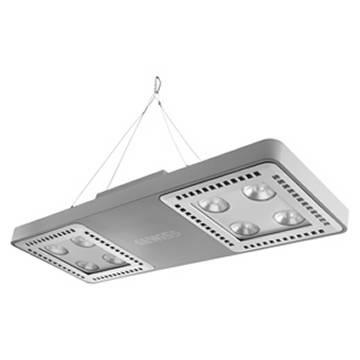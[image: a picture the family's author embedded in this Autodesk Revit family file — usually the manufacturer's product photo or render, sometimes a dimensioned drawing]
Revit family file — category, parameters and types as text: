
# Revit family: Lighting-Industrial-GEWISS-SMART[4]HLO_HIGHBAYS-LED_2M
name_source: partatom
category: Apparecchi per illuminazione
units: mm (PartAtom-declared; Revit-internal decimal feet)

## family parameters
Basato su piano di lavoro = Sì
Condiviso = No
Numero OmniClass = 23.80.70.00
Punto di calcolo locali = No
Quota connettore circolare = Usa diametro
Sempre verticale = No
Sorgente d'illuminazione = No
Taglio con vuoti quando caricato = No
Tipo di parte = Normale
Titolo OmniClass = Lighting

## types (36) — shared parameters
Application = Internal
Body = PA6 "Halogen Free" loaded fibreglass
Carico apparente = 97 VA
Catalogue = LIGHTING
Classification: = -
Classificazione = Lighting
Color Rendering Index = CRI-80
Colour = Grey RAL 7035
Colour : = Grey RAL 7035
Commenti sul wattaggio = 97W
Context = Lighting for industries and sports facilities
Control System = ON / OFF
Control System : = ON / OFF
DIN 18032-3 certification = With Bracket - Rope Kit + terminal&nbsp;(in approval)
Device with reduced surface temperature = Yes
Dist_sorg_lum = 10 mm  [stored 0.0328084 ft]
Driver = Included
Driver Box = Built-in
Electrocod = 2444
Eletrical and lighting features = -
External screw = Stainless steel
Fixing = -
Gasket = anti-aging silicone
General information = -
Glow Wire Test : = 850 °C
IDF = 87744efe-63fb-4f16-8ca3-e5681c99f1f6
IDT = d6c0a54b56be4af78e01cdd4bdcb8af8
IP degree = IP66
IPEA = -
Immagine tipo = GWL1311.jpg
Installationa and maintenance = -
Insulation class = I
LED Maintenance = Non-replaceable
Lampada = LED
Larghezza = 254 mm
Lifetime = L90B10 (Tq+25°C) = 70.000 h - L90B10 (Tq+50°C) = 35.000 h
Locking Hook = -
Luminaire = LED Industrial ReflectorÂ
Lunghezza = 699 mm  [stored 2.29331 ft]
Mascherina = <Per categoria>
Materials = -
Maximum surface exposed to the wind : = 0,184 m²
Motore = <Per categoria>
Mouting and installation = Ceiling - Wallmounting - Suspension
Operating temperature : = -30°C ÷ +50 °C
Optic Maintenance = Non-replaceable
Optic and illuminating features = -
Overvoltage protection = DM 6kV / CM 6kV
Photobiological Risk Class = RG0
Produttore = GEWISS S.p.A.
Prospetto di default = 1219 mm
Rated frequency (Hz) = 50/60 Hz
Shield type = Tempered glass Thickness 4mm
Shock resistance = IK08
Spessore plafoniera = 40 mm  [stored 0.131234 ft]
Standard Deviation Colour Matching = SDCM = 3
Standard- = EN 60598-1 ; EN 60598-2-1 ; EN 60598-2-24
Standards and approvals = -
Stocking temperature = -40 +70 °C
Struttura plafoniera = <Per categoria>
Supply voltage = 220 - 240 V
System power = 125W
Technical sheet = https://www.gewiss.com
Tilt- = With bracket accessory
Trasformatore = <Per categoria>
Type of light source = LED - Not replaceable
URL = https://www.gewiss.com
Unique digital code (Datamatrix) = Datamatrix
Version file RFA = 20.11
Voltaggio = 230 V
Warranty = 5 years
Weight (kg): = 6,5
Wiring = With GW connect watertight connector

## per-type parameters (varying)
| type | Colour temperature | Descrizione | Efficiency (lm/W) | Lumen output (lm) | Modello | Optic | Optic : | SEO | Unified Glare Rating |
| GWS4222BF840 - SMART4HB 2M C.PAS.ON/OFF HLO 30° 40K | 4000K | SMART[4]HB 2M C.PAS.ON/OFF HLO 30° 40K | 141 | 17600 | GWS4222BF840 | 30° | Metallic PC reflector and PMMA lenses |  | UGR - 19 |
| GWS4220BC840 - SMART4HB 2M ST.AL.ON/OFF HLO ASI.40K | 4000K | SMART[4]HB 2M ST.AL.ON/OFF HLO ASI.40K | 128 | 16000 | GWS4220BC840 | Asymmetrical | Metallic PC reflector and PMMA lenses | High bay | - |
| GWS4222BC857 - SMART4HB 2M C.PAS.ON/OFF HLO ASI.57K | 5700K | SMART[4]HB 2M C.PAS.ON/OFF HLO ASI.57K | 128 | 16000 | GWS4222BC857 | Asymmetrical | Metallic PC reflector and PMMA lenses | High bay | - |
| GWS4220BP857 - SMART4HB 2M ST.AL.ON/OFF HLO 90° 57K | 5700K | SMART[4]HB 2M ST.AL.ON/OFF HLO 90° 57K | 144 | 18000 | GWS4220BP857 | 90° | Metallic PC reflector and PMMA lenses |  | UGR - 25 |
| GWS4222BF857 - SMART4HB 2M C.PAS.ON/OFF HLO 30° 57K | 5700K | SMART[4]HB 2M C.PAS.ON/OFF HLO 30° 57K | 141 | 17600 | GWS4222BF857 | 30° | Metallic PC reflector and PMMA lenses |  | UGR - 19 |
| GWS4220BH830 - SMART4HB 2M ST.AL.ON/OFF HLO 60° 30K | 3000K | SMART[4]HB 2M ST.AL.ON/OFF HLO 60° 30K | 135 | 16900 | GWS4220BH830 | 60° | Metallic PC reflector and PMMA lenses |  | UGR - 22 |
| GWS4220BQ857 - SMART4HB 2M ST.AL.ON/OFF HLO ELL.57K | 5700K | SMART[4]HB 2M ST.AL.ON/OFF HLO ELL.57K | 128 | 16000 | GWS4220BQ857 | Elliptical | Metallic PC reflector and PMMA lenses | High bay | - |
| GWS4220BF857 - SMART4HB 2M ST.AL.ON/OFF HLO 30° 57K | 5700K | SMART[4]HB 2M ST.AL.ON/OFF HLO 30° 57K | 141 | 17600 | GWS4220BF857 | 30° | Metallic PC reflector and PMMA lenses |  | UGR - 19 |
| GWS4220BF840 - SMART4HB 2M ST.AL.ON/OFF HLO 30° 40K | 4000K | SMART[4]HB 2M ST.AL.ON/OFF HLO 30° 40K | 141 | 17600 | GWS4220BF840 | 30° | Metallic PC reflector and PMMA lenses |  | UGR - 19 |
| GWS4220BA840 - SMART4HB 2M ST.AL.ON/OFF HLO ARR.40K | 4000K | SMART[4]HB 2M ST.AL.ON/OFF HLO ARR.40K | 144 | 18000 | GWS4220BA840 | Array | Metallized polycarbonate reflector |  | - |
| GWS4222BH840 - SMART4HB 2M C.PAS.ON/OFF HLO 60° 40K | 4000K | SMART[4]HB 2M C.PAS.ON/OFF HLO 60° 40K | 142 | 17700 | GWS4222BH840 | 60° | Metallic PC reflector and PMMA lenses |  | UGR - 22 |
| GWS4222BA840 - SMART4HB 2M C.PAS.ON/OFF HLO ARR.40K | 4000K | SMART[4]HB 2M C.PAS.ON/OFF HLO ARR.40K | 144 | 18000 | GWS4222BA840 | Array | Metallized polycarbonate reflector |  | - |
| GWS4220BC857 - SMART4HB 2M ST.AL.ON/OFF HLO ASI.57K | 5700K | SMART[4]HB 2M ST.AL.ON/OFF HLO ASI.57K | 128 | 16000 | GWS4220BC857 | Asymmetrical | Metallic PC reflector and PMMA lenses | High bay | - |
| GWS4220BA830 - SMART4HB 2M ST.AL.ON/OFF HLO ARR.30K | 3000K | SMART[4]HB 2M ST.AL.ON/OFF HLO ARR.30K | 138 | 17200 | GWS4220BA830 | Array | Metallized polycarbonate reflector |  | - |
| GWS4222BP857 - SMART4HB 2M C.PAS.ON/OFF HLO 90° 57K | 5700K | SMART[4]HB 2M C.PAS.ON/OFF HLO 90° 57K | 144 | 18000 | GWS4222BP857 | 90° | Metallic PC reflector and PMMA lenses |  | UGR - 25 |
| GWS4222BF830 - SMART4HB 2M C.PAS.ON/OFF HLO 30° 30K | 3000K | SMART[4]HB 2M C.PAS.ON/OFF HLO 30° 30K | 134 | 16800 | GWS4222BF830 | 30° | Metallic PC reflector and PMMA lenses |  | UGR - 19 |
| GWS4222BC840 - SMART4HB 2M C.PAS.ON/OFF HLO ASI.40K | 4000K | SMART[4]HB 2M C.PAS.ON/OFF HLO ASI.40K | 128 | 16000 | GWS4222BC840 | Asymmetrical | Metallic PC reflector and PMMA lenses | High bay | - |
| GWS4222BH857 - SMART4HB 2M C.PAS.ON/OFF HLO 60° 57K | 5700K | SMART[4]HB 2M C.PAS.ON/OFF HLO 60° 57K | 142 | 17700 | GWS4222BH857 | 60° | Metallic PC reflector and PMMA lenses |  | UGR - 22 |
| GWS4220BQ830 - SMART4HB 2M ST.AL.ON/OFF HLO ELL.30K | 3000K | SMART[4]HB 2M ST.AL.ON/OFF HLO ELL.30K | 122 | 15300 | GWS4220BQ830 | Elliptical | Metallic PC reflector and PMMA lenses | High bay | - |
| GWS4222BA857 - SMART4HB 2M C.PAS.ON/OFF HLO ARR.57K | 5700K | SMART[4]HB 2M C.PAS.ON/OFF HLO ARR.57K | 144 | 18000 | GWS4222BA857 | Array | Metallized polycarbonate reflector |  | - |
| GWS4222BQ857 - SMART4HB 2M C.PAS.ON/OFF HLO ELL.57K | 5700K | SMART[4]HB 2M C.PAS.ON/OFF HLO ELL.57K | 128 | 16000 | GWS4222BQ857 | Elliptical | Metallic PC reflector and PMMA lenses | High bay | - |
| GWS4222BP830 - SMART4HB 2M C.PAS.ON/OFF HLO 90° 30K | 3000K | SMART[4]HB 2M C.PAS.ON/OFF HLO 90° 30K | 138 | 17200 | GWS4222BP830 | 90° | Metallic PC reflector and PMMA lenses |  | UGR - 25 |
| GWS4220BH857 - SMART4HB 2M ST.AL.ON/OFF HLO 60° 57K | 5700K | SMART[4]HB 2M ST.AL.ON/OFF HLO 60° 57K | 142 | 17700 | GWS4220BH857 | 60° | Metallic PC reflector and PMMA lenses |  | UGR - 22 |
| GWS4220BP840 - SMART4HB 2M ST.AL.ON/OFF HLO 90° 40K | 4000K | SMART[4]HB 2M ST.AL.ON/OFF HLO 90° 40K | 144 | 18000 | GWS4220BP840 | 90° | Metallic PC reflector and PMMA lenses |  | UGR - 25 |
| GWS4222BH830 - SMART4HB 2M C.PAS.ON/OFF HLO 60° 30K | 3000K | SMART[4]HB 2M C.PAS.ON/OFF HLO 60° 30K | 135 | 16900 | GWS4222BH830 | 60° | Metallic PC reflector and PMMA lenses |  | UGR - 22 |
| GWS4220BH840 - SMART4HB 2M ST.AL.ON/OFF HLO 60° 40K | 4000K | SMART[4]HB 2M ST.AL.ON/OFF HLO 60° 40K | 142 | 17700 | GWS4220BH840 | 60° | Metallic PC reflector and PMMA lenses |  | UGR - 22 |
| GWS4222BQ830 - SMART4HB 2M C.PAS.ON/OFF HLO ELL.30K | 3000K | SMART[4]HB 2M C.PAS.ON/OFF HLO ELL.30K | 122 | 15300 | GWS4222BQ830 | Elliptical | Metallic PC reflector and PMMA lenses | High bay | - |
| GWS4220BC830 - SMART4HB 2M ST.AL.ON/OFF HLO ASI.30K | 3000K | SMART[4]HB 2M ST.AL.ON/OFF HLO ASI.30K | 122 | 15300 | GWS4220BC830 | Asymmetrical | Metallic PC reflector and PMMA lenses | High bay | - |
| GWS4220BQ840 - SMART4HB 2M ST.AL.ON/OFF HLO ELL.40K | 4000K | SMART[4]HB 2M ST.AL.ON/OFF HLO ELL.40K | 128 | 16000 | GWS4220BQ840 | Elliptical | Metallic PC reflector and PMMA lenses | High bay | - |
| GWS4220BF830 - SMART4HB 2M ST.AL.ON/OFF HLO 30° 30K | 3000K | SMART[4]HB 2M ST.AL.ON/OFF HLO 30° 30K | 134 | 16800 | GWS4220BF830 | 30° | Metallic PC reflector and PMMA lenses |  | UGR - 19 |
| GWS4222BC830 - SMART4HB 2M C.PAS.ON/OFF HLO ASI.30K | 3000K | SMART[4]HB 2M C.PAS.ON/OFF HLO ASI.30K | 122 | 15300 | GWS4222BC830 | Asymmetrical | Metallic PC reflector and PMMA lenses | High bay | - |
| GWS4222BQ840 - SMART4HB 2M C.PAS.ON/OFF HLO ELL.40K | 4000K | SMART[4]HB 2M C.PAS.ON/OFF HLO ELL.40K | 128 | 16000 | GWS4222BQ840 | Elliptical | Metallic PC reflector and PMMA lenses | High bay | - |
| GWS4220BA857 - SMART4HB 2M ST.AL.ON/OFF HLO ARR.57K | 5700K | SMART[4]HB 2M ST.AL.ON/OFF HLO ARR.57K | 144 | 18000 | GWS4220BA857 | Array | Metallized polycarbonate reflector |  | - |
| GWS4222BA830 - SMART4HB 2M C.PAS.ON/OFF HLO ARR.30K | 3000K | SMART[4]HB 2M C.PAS.ON/OFF HLO ARR.30K | 138 | 17200 | GWS4222BA830 | Array | Metallized polycarbonate reflector |  | - |
| GWS4222BP840 - SMART4HB 2M C.PAS.ON/OFF HLO 90° 40K | 4000K | SMART[4]HB 2M C.PAS.ON/OFF HLO 90° 40K | 144 | 18000 | GWS4222BP840 | 90° | Metallic PC reflector and PMMA lenses |  | UGR - 25 |
| GWS4220BP830 - SMART4HB 2M ST.AL.ON/OFF HLO 90° 30K | 3000K | SMART[4]HB 2M ST.AL.ON/OFF HLO 90° 30K | 138 | 17200 | GWS4220BP830 | 90° | Metallic PC reflector and PMMA lenses |  | UGR - 25 |

note: [stored X ft] marks values corroborated as IEEE doubles in the binary element streams (Revit-internal decimal feet)

## geometry (parser evidence)
native form markers: Blend x4, Sweep x3
no freeform markers — native parametric forms only
